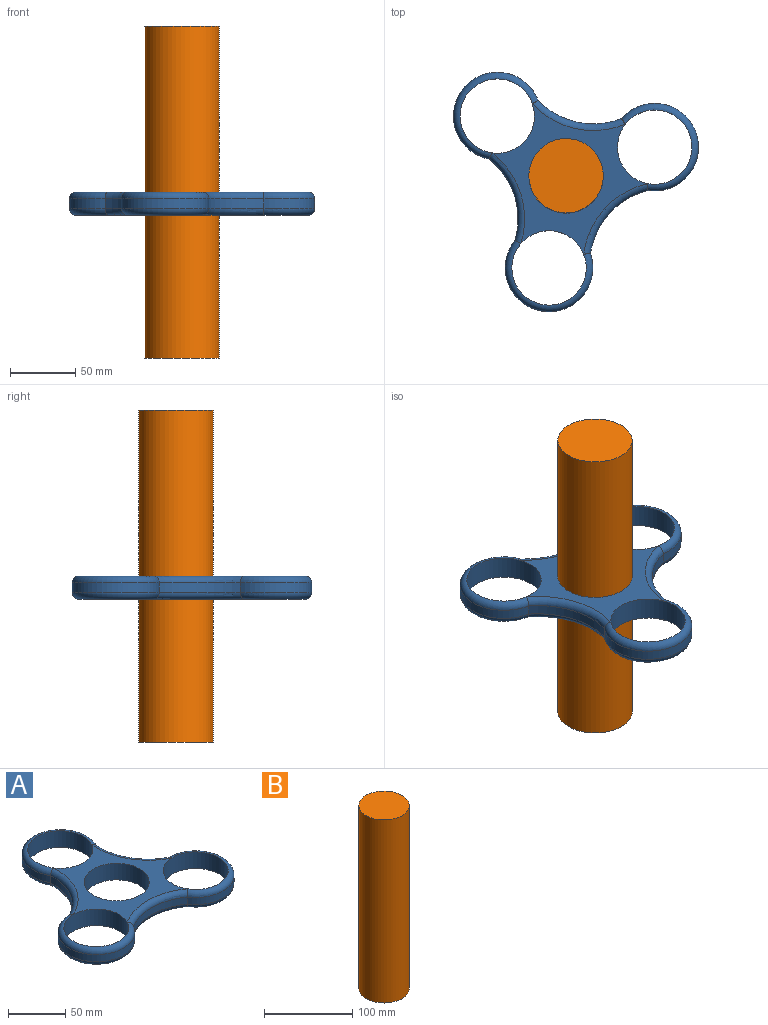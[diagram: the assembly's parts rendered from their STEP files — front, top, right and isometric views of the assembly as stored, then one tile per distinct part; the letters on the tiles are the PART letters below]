
ASSEMBLY  parts=2 mates=1
PART A: 24 faces, bbox 195.3x179x17.8 mm
  f0: cylinder r=58.36mm len=57.27mm, axis (0,0,1), area 527.8mm2, adj f1,f9,f13,f19
  f1: cylinder r=33.53mm len=67.06mm, axis (0,0,1), area 1061.6mm2, adj f0,f2,f12,f18
  f2: cylinder r=58.36mm len=55.76mm, axis (0,0,1), area 527.8mm2, adj f1,f3,f14,f20
  f3: cylinder r=33.53mm len=67.03mm, axis (0,0,1), area 1061.6mm2, adj f2,f4,f16,f22
  f4: cylinder r=58.36mm len=65.26mm, axis (0,0,1), area 527.8mm2, adj f3,f9,f17,f23
  f5: cylinder r=28.45mm len=56.9mm, axis (0,0,1), area 3178.1mm2, adj f10,f11
  f6: cylinder r=28.45mm len=56.9mm, axis (0,0,1), area 3178.1mm2, adj f10,f11,f12,f18
  f7: cylinder r=28.45mm len=56.9mm, axis (0,0,1), area 3178.1mm2, adj f10,f11,f15,f21
  f8: cylinder r=28.45mm len=56.9mm, axis (0,0,1), area 3178.1mm2, adj f10,f11,f16,f22
  f9: cylinder r=33.53mm len=67.06mm, axis (0,0,1), area 1061.6mm2, adj f0,f4,f15,f21
  f10: plane 121.58x106.7mm, normal (0,0,-1), area 3797.3mm2, adj f5,f6,f7,f8,f19,f20,f23
  f11: plane 121.58x106.7mm, normal (0,0,1), area 3797.3mm2, adj f5,f6,f7,f8,f13,f14,f17
  f12: torus R=28.45mm, axis (0,0,1), area 1056.8mm2, adj f1,f6,f13,f14
  f13: torus R=63.44mm, axis (0,0,1), area 577mm2, adj f0,f11,f12,f15
  f14: torus R=63.44mm, axis (0,0,1), area 577mm2, adj f2,f11,f12,f16
  f15: torus R=28.45mm, axis (0,0,1), area 1056.8mm2, adj f7,f9,f13,f17
  f16: torus R=28.45mm, axis (0,0,1), area 1056.8mm2, adj f3,f8,f14,f17
  f17: torus R=63.44mm, axis (0,0,1), area 577mm2, adj f4,f11,f15,f16
  f18: torus R=28.45mm, axis (0,0,1), area 1056.8mm2, adj f1,f6,f19,f20
  f19: torus R=63.44mm, axis (0,0,1), area 577mm2, adj f0,f10,f18,f21
  f20: torus R=63.44mm, axis (0,0,1), area 577mm2, adj f2,f10,f18,f22
  f21: torus R=28.45mm, axis (0,0,1), area 1056.8mm2, adj f7,f9,f19,f23
  f22: torus R=28.45mm, axis (0,0,1), area 1056.8mm2, adj f3,f8,f20,f23
  f23: torus R=63.44mm, axis (0,0,1), area 577mm2, adj f4,f10,f21,f22
PART B: 3 faces, bbox 56.9x56.9x254 mm
  f0: cylinder r=28.45mm len=254mm, axis (0,0,-1), area 45401mm2, adj f1,f2
  f1: plane 56.9x56.9mm, normal (0,0,1), area 2542.5mm2, adj f0
  f2: plane 56.9x56.9mm, normal (0,0,-1), area 2542.5mm2, adj f0
PLACE A rot(axis=(0,0,1),48.9deg) t=(-3.06,-96.66,62.04)mm
PLACE B t=(-3.06,-96.66,62.04)mm fixed
MATE revolute A.f5 <-> B.f0  axis (0,0,1) through (-3.06,-96.66,62.04)mm
